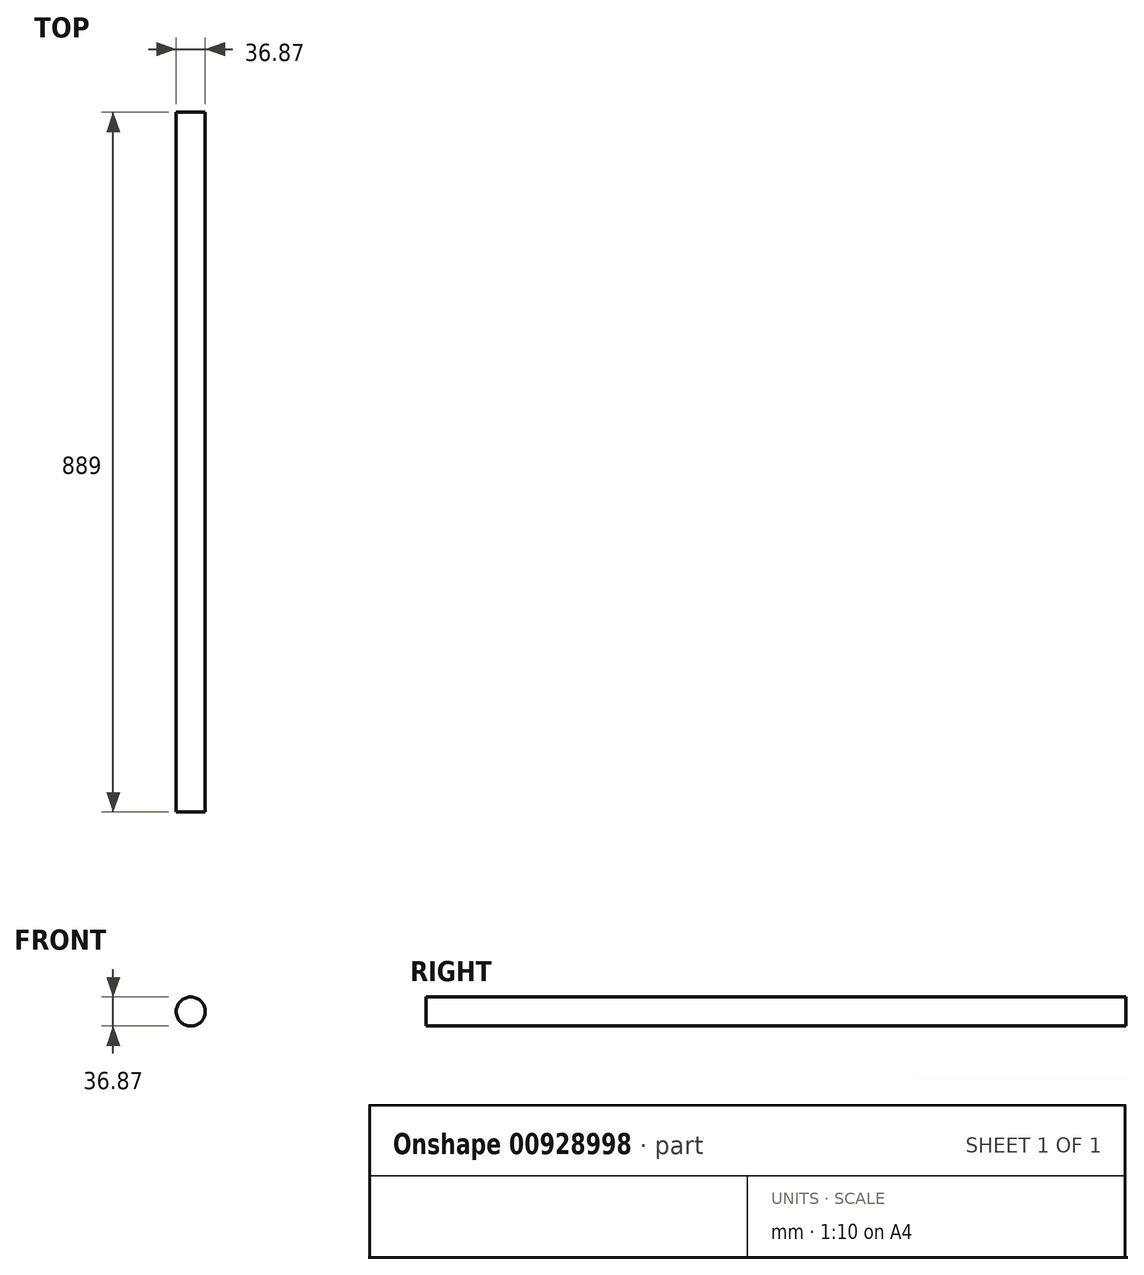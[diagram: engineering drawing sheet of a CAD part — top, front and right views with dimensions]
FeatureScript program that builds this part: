
annotation { "Feature Type Name" : "Feature", "Feature Type Description" : "" }
export const myFeature = defineFeature(function(context is Context, id is Id, definition is map)
    precondition{}
    {
        {
            var Q0;
            Q0=qCreatedBy(makeId("Front.planeOp"),FACE);
            var sketch = newSketch(context, id + "F0", { "sketchPlane" : qUnion([Q0])});
            skCircle(sketch, "E0", {"center": v(-47.46, 33.77) * mm, "radius": 18.43 * mm});
            skSolve(sketch);
        }
        {
            var Q0;
            Q0 = qSketchRegion(id + "F0", true);
            extrude(context, id + "F1", {"entities" : qUnion([Q0]), "depth" : 889 * mm, "offsetDistance" : 25.4 * mm});
        }
    });
